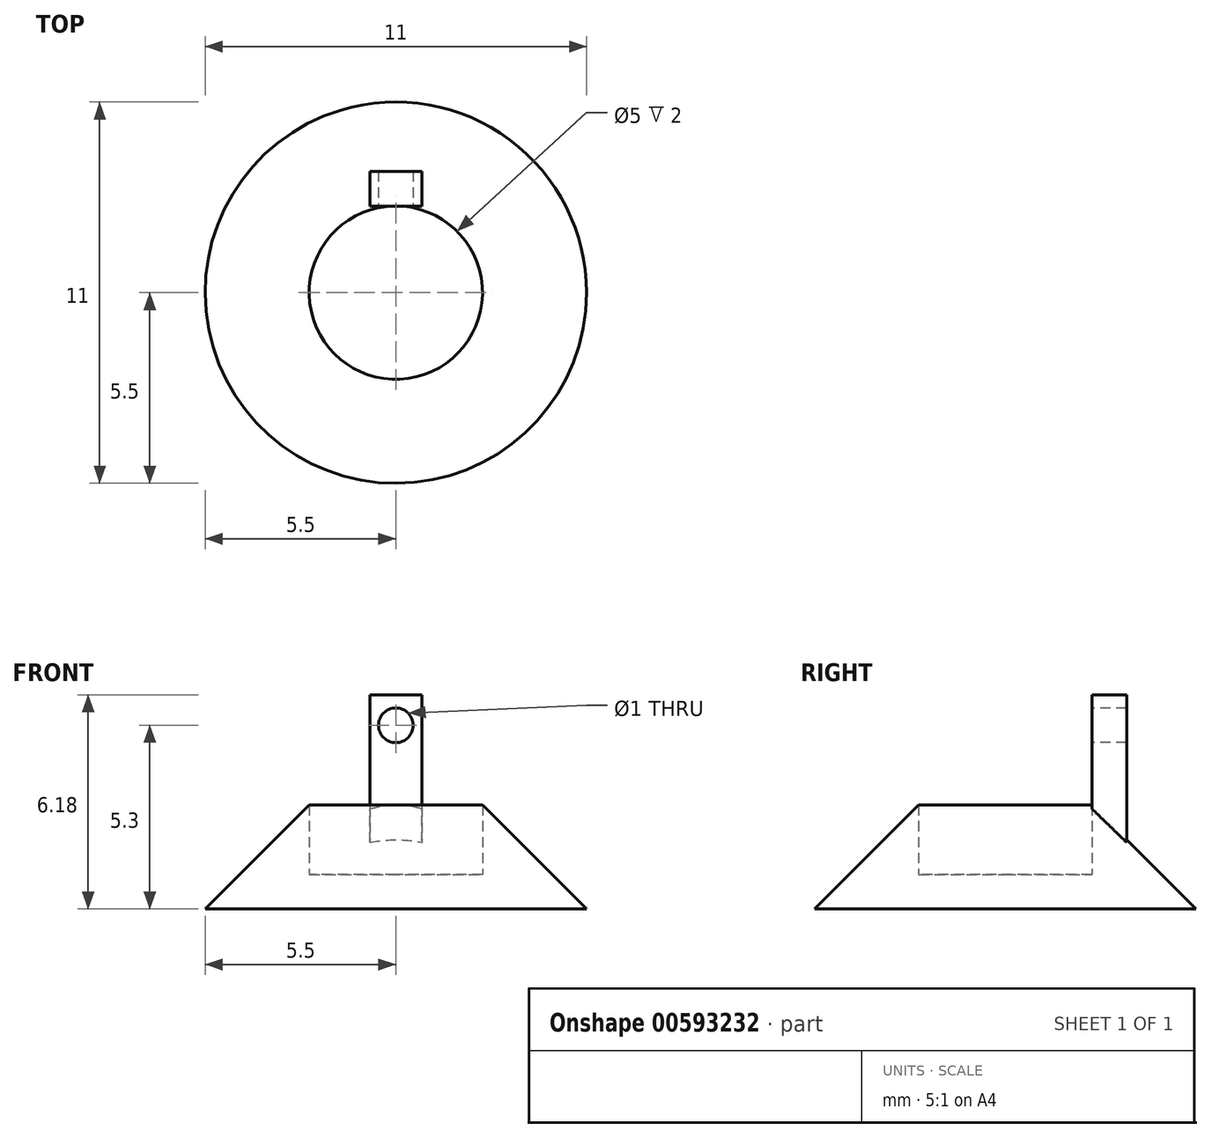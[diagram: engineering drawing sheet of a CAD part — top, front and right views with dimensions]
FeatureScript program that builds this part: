
annotation { "Feature Type Name" : "Feature", "Feature Type Description" : "" }
export const myFeature = defineFeature(function(context is Context, id is Id, definition is map)
    precondition{}
    {
        {
            var Q0;
            Q0=qCreatedBy(makeId("Top.planeOp"),FACE);
            var sketch = newSketch(context, id + "F0", { "sketchPlane" : qUnion([Q0])});
            skCircle(sketch, "E0", {"center": v(0, 0) * mm, "radius": 5.5 * mm});
            skCircle(sketch, "E1", {"center": v(0, 0) * mm, "radius": 2.5 * mm});
            skSolve(sketch);
        }
        {
            var Q0;
            Q0 = qSketchRegion(id + "F0", true);
            extrude(context, id + "F1", {"entities" : qUnion([Q0]), "depth" : 3 * mm, "offsetDistance" : 25 * mm});
        }
        {
            var Q0;
            Q0=makeQuery(id+"F0.imprint","IMPRINT",FACE,{"disambiguationData":[TD([[makeQuery(id+"F0.imprint","IMPRINT",EDGE,{"derivedFrom":sQuery(id+"F0.wireOp",EDGE,"E1")}),1.0]])]});
            extrude(context, id + "F2", {"entities" : qUnion([Q0]), "operationType" : NewBodyOperationType.ADD, "depth" : 1 * mm, "offsetDistance" : 25 * mm});
        }
        {
            var Q0;
            Q0=makeQuery(id+"F1.opExtrude","CAP_EDGE",EDGE,{"disambiguationData":[OSD([sQuery(id+"F0.wireOp",EDGE,"E0")])],"isStart":false});
            chamfer(context, id + "F3", {"entities" : qUnion([Q0]), "width" : 3 * mm, "tangentPropagation" : true});
        }
        {
            var Q0;
            Q0=qCreatedBy(makeId("Top.planeOp"),FACE);
            var sketch = newSketch(context, id + "F4", { "sketchPlane" : qUnion([Q0])});
            skLineSegment(sketch, "E2.bottom", {"start": v(-0.75, 3.5) * mm, "end": v(0.75, 3.5) * mm});
            skLineSegment(sketch, "E2.top", {"start": v(-0.75, 2.5) * mm, "end": v(0.75, 2.5) * mm});
            skLineSegment(sketch, "E2.left", {"start": v(-0.75, 3.5) * mm, "end": v(-0.75, 2.5) * mm});
            skLineSegment(sketch, "E2.right", {"start": v(0.75, 3.5) * mm, "end": v(0.75, 2.5) * mm});
            skSolve(sketch);
        }
        {
            var Q0;
            Q0 = qSketchRegion(id + "F4", true);
            extrude(context, id + "F5", {"entities" : qUnion([Q0]), "operationType" : NewBodyOperationType.ADD, "depth" : 6.18 * mm, "offsetDistance" : 25 * mm});
        }
        {
            var Q0;
            Q0=makeQuery(id+"F5.opExtrude","SWEPT_FACE",FACE,{"disambiguationData":[OSD([sQuery(id+"F4.wireOp",EDGE,"E2.top")])]});
            var sketch = newSketch(context, id + "F6", { "sketchPlane" : qUnion([Q0])});
            skCircle(sketch, "E3", {"center": v(0, 5.3) * mm, "radius": 0.5 * mm});
            skSolve(sketch);
        }
        {
            var Q0;
            Q0 = qSketchRegion(id + "F6", true);
            extrude(context, id + "F7", {"entities" : qUnion([Q0]), "operationType" : NewBodyOperationType.REMOVE, "oppositeDirection" : true, "depth" : 25 * mm, "offsetDistance" : 25 * mm});
        }
    });
